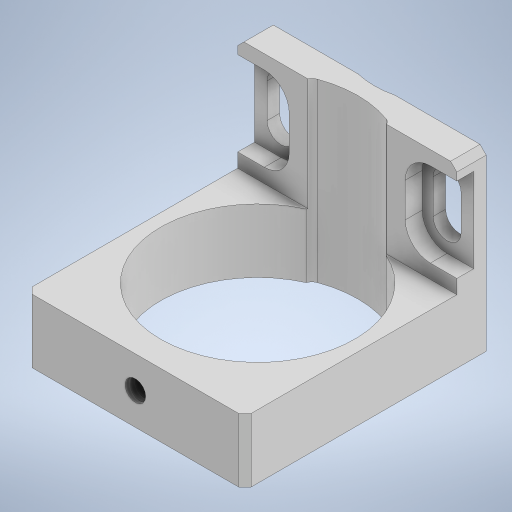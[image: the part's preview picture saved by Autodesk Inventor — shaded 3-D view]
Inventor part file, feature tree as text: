
AUTODESK INVENTOR PART (.ipt)
format: ipt  version: 2024.2 (Build 282272000, 272)  size: 552,960 bytes
history: native  units: in
note: dims shown in document units (in); Inventor stores cm internally (conversion verified against a paired STEP export)
features: extrude x8, sketch x2, hole x2, chamfer x1
ambient origin geometry x8: Origin, YZ Plane, XZ Plane, XY Plane, X Axis, Y Axis, Z Axis, Center Point
bodies: Body1 (feature_tree)
feature tree (13):
  extrude  "Extrusion3"  Depth=0.6906in
  extrude  "Extrusion4"  Depth=0.6906in TaperAngle=0.0deg
  sketch  "Sketch9"  dims[d24=1.1102in d26=0.6906in]
  extrude  "Extrusion6"  TaperAngle=0.0deg  [1 undecoded]
  extrude  "Extrusion7"  TaperAngle=0.0deg  [1 undecoded]
  hole  "Hole3"  [1 undecoded]
  chamfer  "Chamfer10"  [1 undecoded]
  extrude  "Extrusion11"  Depth=0.6906in TaperAngle=0.0deg
  hole  "Hole4"  [1 undecoded]
  extrude  "Extrusion15"  Depth=0.6906in TaperAngle=0.0deg
  extrude  "Extrusion16"  Depth=0.6906in
  extrude  "Extrusion19"  Depth=0.7087in
  sketch  "Sketch26"  dims[d28=0.4016in d29=0.185in d30=0.0in d31=0.0in d32=0.0in d33=0.0in d34=0.0in d35=1.3358in d36=0.0in d77=0.0827in d78=0.0in d85=0.0827in d86=0.328in d87=0.297in d88=0.11in d89=90.0deg d90=0.0827in d91=0.0in d93=0.3622in d94=0.0in d131=0.3543in d183=0.7087in d185=0.0886in d186=0.2165in d187=0.0in d188=0.3243in d189=0.0413in d190=0.0392in d191=0.0in d192=0.1969in d193=0.0394in d194=0.0787in d195=45.0deg d196=0.0in d197=1.0in d199=0.3937in d200=0.0in d201=0.75in d203=0.0in d204=0.1969in d205=0.13in d206=0.328in d207=0.1575in d208=0.0787in d209=90.0deg d211=0.0in d212=0.0in d213=0.2008in d214=0.4016in d224=0.4862in d225=0.6906in d226=1.2433in d227=0.1374in d228=0.1374in d229=0.1201in d230=0.1201in d231=0.5616in d232=0.5616in d251=0.7087in d252=0.3543in d253=0.4827in d254=0.1673in d255=0.1772in d256=0.2165in d257=0.7087in d258=0.4827in d259=0.3543in d261=0.1772in d262=0.2165in d263=0.0in d264=0.0in d265=0.3543in d266=0.1673in d267=0.3543in d269=0.315in d270=0.2165in d271=0.315in d272=0.2165in d273=0.1063in d274=0.0in d293=0.1673in d295=0.1673in d309=0.75in d311=0.002in d314=1.2236in d315=0.75in d316=0.6906in d317=1.263in d318=0.1374in d319=0.1374in d320=0.1201in d321=0.1201in d322=0.5715in d323=0.5715in d324=0.75in d325=1.374in d326=0.002in d327=0.0in d328=0.0in]
note: 5 required parameter values undecoded (feature->parameter linkage not recoverable at this tier; creation-order binding heuristic only, values carry confidence <= 0.55)
